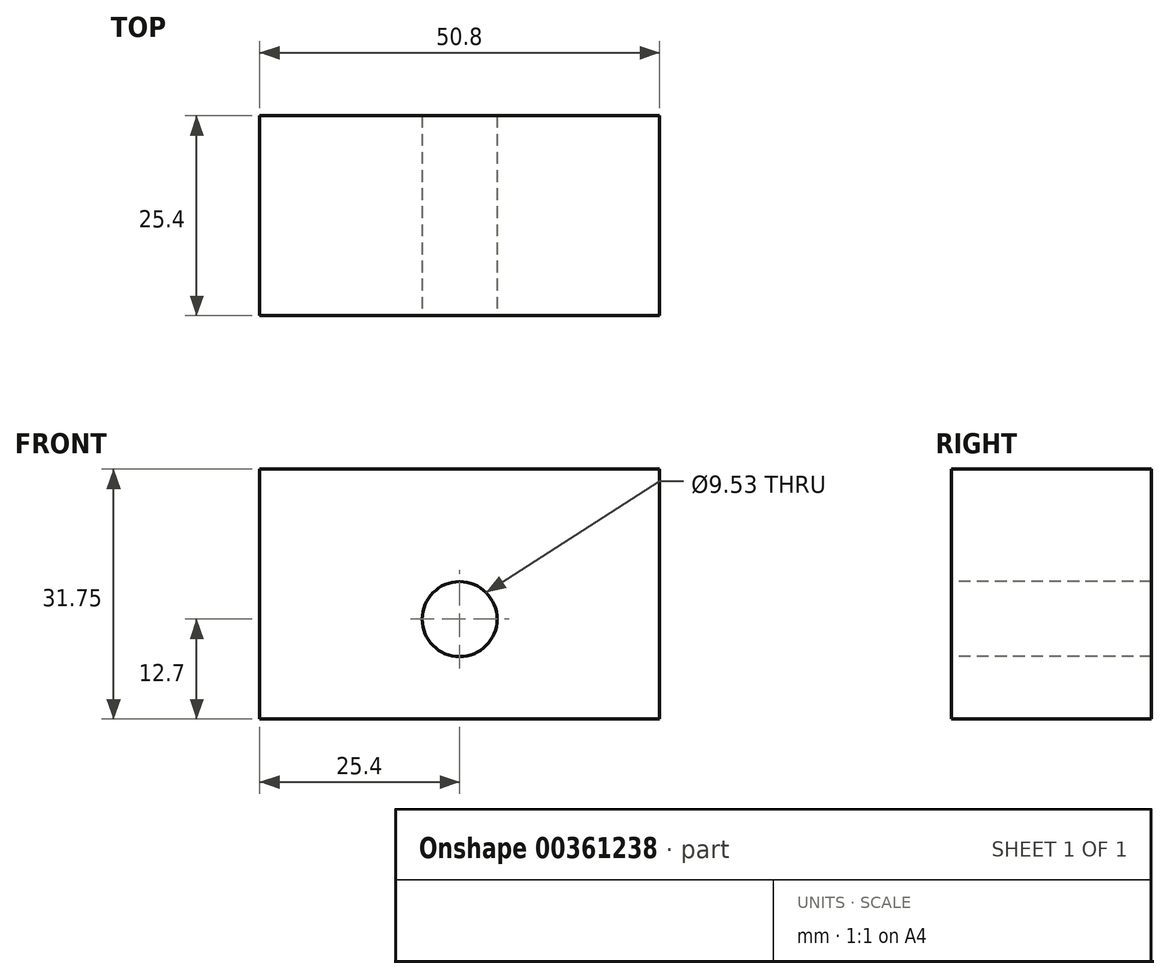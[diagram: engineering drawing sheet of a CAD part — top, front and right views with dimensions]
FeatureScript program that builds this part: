
annotation { "Feature Type Name" : "Feature", "Feature Type Description" : "" }
export const myFeature = defineFeature(function(context is Context, id is Id, definition is map)
    precondition{}
    {
        {
            var Q0;
            Q0=qCreatedBy(makeId("Front.planeOp"),FACE);
            var sketch = newSketch(context, id + "F0", { "sketchPlane" : qUnion([Q0])});
            skLineSegment(sketch, "E0.bottom", {"start": v(0, 0) * mm, "end": v(50.8, 0) * mm});
            skLineSegment(sketch, "E0.top", {"start": v(0, 31.75) * mm, "end": v(50.8, 31.75) * mm});
            skLineSegment(sketch, "E0.left", {"start": v(0, 0) * mm, "end": v(0, 31.75) * mm});
            skLineSegment(sketch, "E0.right", {"start": v(50.8, 0) * mm, "end": v(50.8, 31.75) * mm});
            skSolve(sketch);
        }
        {
            var Q0;
            Q0=makeQuery(id+"F0.imprint","IMPRINT",FACE,{"disambiguationData":[TD([[makeQuery(id+"F0.imprint","IMPRINT",EDGE,{"derivedFrom":sQuery(id+"F0.wireOp",EDGE,"E0.bottom")}),1.0]])]});
            extrude(context, id + "F1", {"entities" : qUnion([Q0]), "depth" : 25.4 * mm});
        }
        {
            var Q0;
            Q0=makeQuery(id+"F1.opExtrude","CAP_FACE",FACE,{"disambiguationData":[OSD([sQuery(id+"F0.wireOp",EDGE,"E0.bottom"),sQuery(id+"F0.wireOp",EDGE,"E0.top"),sQuery(id+"F0.wireOp",EDGE,"E0.left"),sQuery(id+"F0.wireOp",EDGE,"E0.right")])],"isStart":false});
            var sketch = newSketch(context, id + "F2", { "sketchPlane" : qUnion([Q0])});
            skCircle(sketch, "E1", {"center": v(25.4, 12.7) * mm, "radius": 4.76 * mm});
            skSolve(sketch);
        }
        {
            var Q0;
            Q0 = qSketchRegion(id + "F2", true);
            extrude(context, id + "F3", {"entities" : qUnion([Q0]), "operationType" : NewBodyOperationType.REMOVE, "endBound" : BoundingType.THROUGH_ALL, "oppositeDirection" : true, "depth" : 25.4 * mm});
        }
    });
